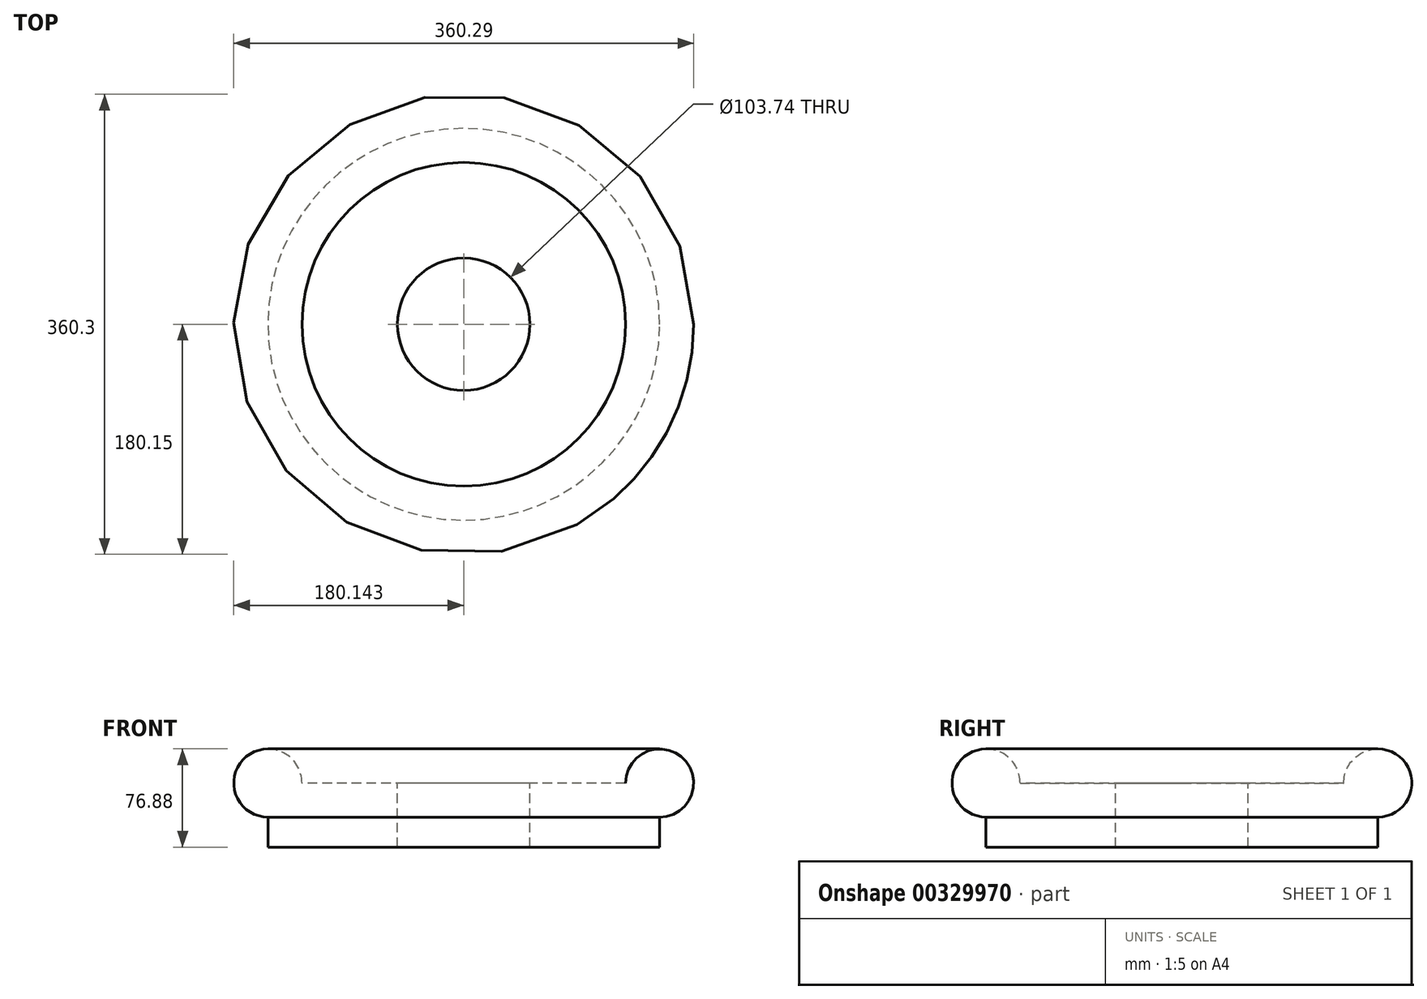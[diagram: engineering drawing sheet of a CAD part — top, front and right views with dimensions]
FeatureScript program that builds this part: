
annotation { "Feature Type Name" : "Feature", "Feature Type Description" : "" }
export const myFeature = defineFeature(function(context is Context, id is Id, definition is map)
    precondition{}
    {
        {
            var Q0;
            Q0=qCreatedBy(makeId("Front.planeOp"),FACE);
            var sketch = newSketch(context, id + "F0", { "sketchPlane" : qUnion([Q0])});
            skLineSegment(sketch, "E0.bottom", {"start": v(-50.32, 23.78) * mm, "end": v(24.59, 23.78) * mm});
            skLineSegment(sketch, "E0.top", {"start": v(-50.32, -26.41) * mm, "end": v(51.27, -26.41) * mm});
            skLineSegment(sketch, "E0.left", {"start": v(-50.32, 23.78) * mm, "end": v(-50.32, -26.41) * mm});
            skLineSegment(sketch, "E0.right", {"start": v(51.27, -2.9) * mm, "end": v(51.27, -26.41) * mm});
            skArc(sketch, "E1", {"start": v(51.27, -2.9) * mm, "mid": v(70.14, 42.65) * mm, "end": v(24.59, 23.78) * mm});
            skLineSegment(sketch, "E2", {"start": v(-102.19, 57.49) * mm, "end": v(-102.19, -63.7) * mm});
            skSolve(sketch);
        }
        {
            var Q0;
            Q0 = qSketchRegion(id + "F0", true);
            var Q1;
            Q1=sQuery(id+"F0.wireOp",EDGE,"E2");
            revolve(context, id + "F1", {"entities" : qUnion([Q0]), "axis" : qUnion([Q1]), "revolveType" : RevolveType.FULL});
        }
    });
